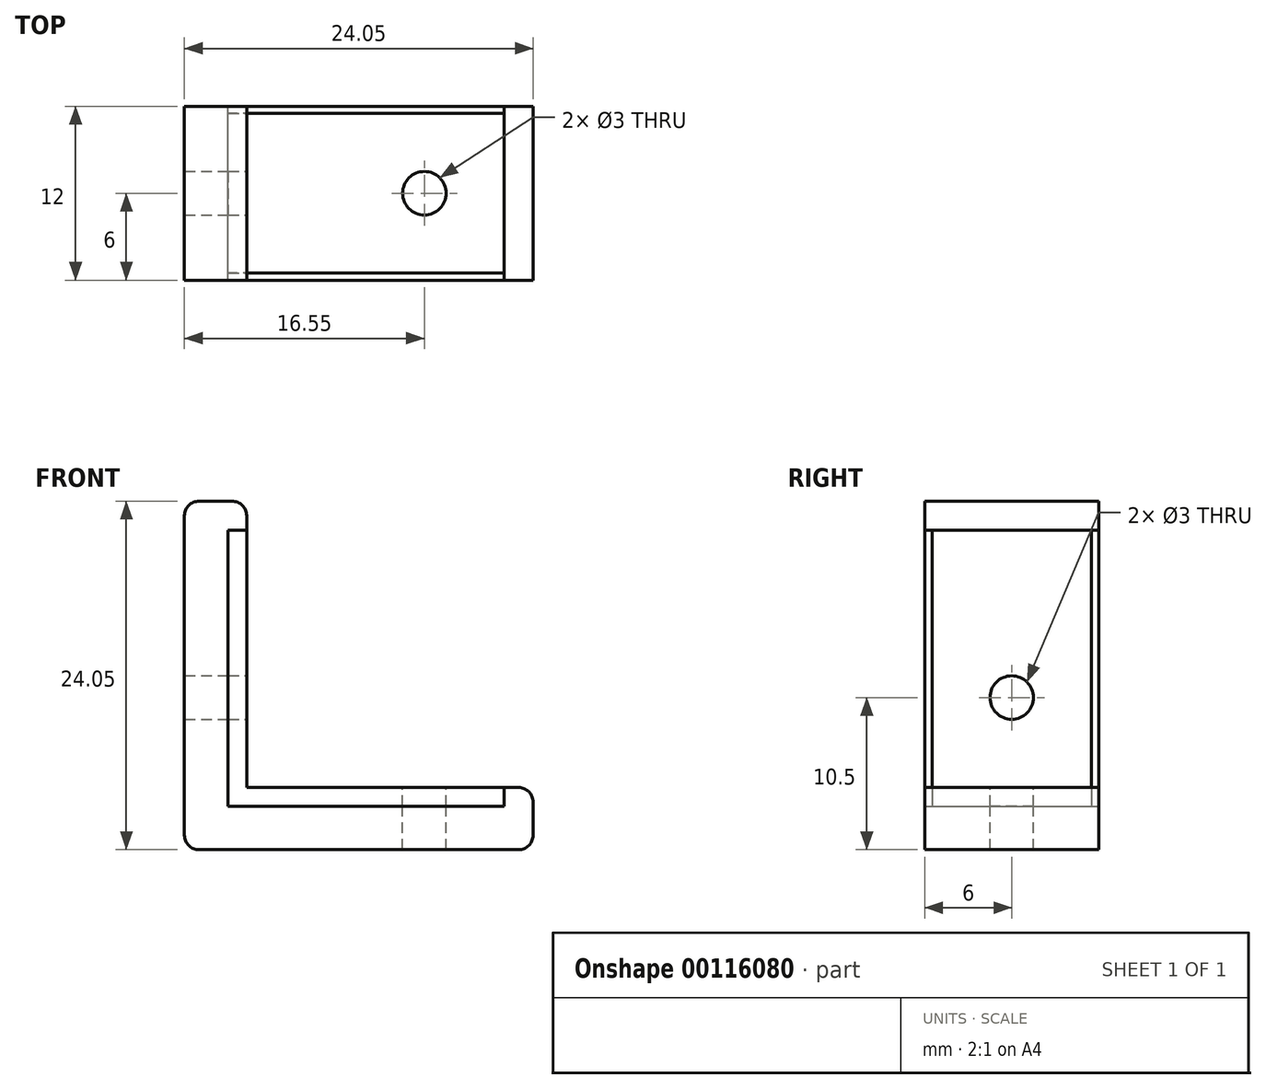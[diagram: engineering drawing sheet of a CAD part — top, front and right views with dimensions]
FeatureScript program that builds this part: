
annotation { "Feature Type Name" : "Feature", "Feature Type Description" : "" }
export const myFeature = defineFeature(function(context is Context, id is Id, definition is map)
    precondition{}
    {
        {
            var Q0;
            Q0=qCreatedBy(makeId("Front.planeOp"),FACE);
            var sketch = newSketch(context, id + "F0", { "sketchPlane" : qUnion([Q0])});
            skLineSegment(sketch, "E0", {"start": v(-29.8, 0) * mm, "end": v(29.8, 0) * mm, "construction": true});
            skLineSegment(sketch, "E1", {"start": v(-26.98, 7.5) * mm, "end": v(40.2, 7.5) * mm, "construction": true});
            skCircle(sketch, "E2", {"center": v(-26.98, 7.5) * mm, "radius": 2.6 * mm, "construction": true});
            skLineSegment(sketch, "E3.bottom", {"start": v(-17.5, 0) * mm, "end": v(17.5, 0) * mm});
            skLineSegment(sketch, "E3.top", {"start": v(-17.5, 6.35) * mm, "end": v(17.5, 6.35) * mm});
            skLineSegment(sketch, "E3.left", {"start": v(-17.5, 1.8) * mm, "end": v(-17.5, 6.35) * mm});
            skLineSegment(sketch, "E3.right", {"start": v(17.5, 0) * mm, "end": v(17.5, 6.35) * mm});
            skLineSegment(sketch, "E4.bottom", {"start": v(-17.4, 6.35) * mm, "end": v(-8.6, 6.35) * mm});
            skLineSegment(sketch, "E4.top", {"start": v(-17.4, 9.85) * mm, "end": v(-8.6, 9.85) * mm});
            skLineSegment(sketch, "E4.left", {"start": v(-17.4, 6.35) * mm, "end": v(-17.4, 9.85) * mm});
            skLineSegment(sketch, "E4.right", {"start": v(-8.6, 6.35) * mm, "end": v(-8.6, 9.85) * mm});
            skLineSegment(sketch, "E5", {"start": v(-13, 6.35) * mm, "end": v(-13, 0) * mm, "construction": true});
            skLineSegment(sketch, "E6", {"start": v(-10.5, 6.35) * mm, "end": v(-10.5, 0) * mm, "construction": true});
            skLineSegment(sketch, "E7.MirrorCS", {"start": v(-15.5, 6.35) * mm, "end": v(-15.5, 0) * mm, "construction": true});
            skLineSegment(sketch, "E8", {"start": v(-17.5, 1.8) * mm, "end": v(-7.5, 1.8) * mm});
            skLineSegment(sketch, "E9", {"start": v(-7.5, 1.8) * mm, "end": v(-7.5, 0) * mm});
            skLineSegment(sketch, "E10.bottom", {"start": v(-2.67, 0) * mm, "end": v(0, 0) * mm});
            skLineSegment(sketch, "E10.top", {"start": v(-2.67, 6.35) * mm, "end": v(0, 6.35) * mm});
            skLineSegment(sketch, "E10.left", {"start": v(-2.67, 0) * mm, "end": v(-2.67, 6.35) * mm});
            skLineSegment(sketch, "E10.right", {"start": v(0, 0) * mm, "end": v(0, 6.35) * mm});
            skLineSegment(sketch, "E11.bottom", {"start": v(9.83, 0) * mm, "end": v(12.5, 0) * mm});
            skLineSegment(sketch, "E11.top", {"start": v(9.83, 6.35) * mm, "end": v(12.5, 6.35) * mm});
            skLineSegment(sketch, "E11.left", {"start": v(9.83, 0) * mm, "end": v(9.83, 6.35) * mm});
            skLineSegment(sketch, "E11.right", {"start": v(12.5, 0) * mm, "end": v(12.5, 6.35) * mm});
            skCircle(sketch, "E12", {"center": v(-26.98, 7.5) * mm, "radius": 4.5 * mm, "construction": true});
            skSolve(sketch);
        }
        {
            var Q0;
            Q0=qCreatedBy(makeId("Front.planeOp"),FACE);
            var sketch = newSketch(context, id + "F1", { "sketchPlane" : qUnion([Q0])});
            skLineSegment(sketch, "E13.0", {"start": v(-7.5, 1.3) * mm, "end": v(-7.5, 0) * mm});
            skLineSegment(sketch, "E14.0", {"start": v(-25.26, 1.3) * mm, "end": v(-7.5, 1.3) * mm});
            skLineSegment(sketch, "E15.0", {"start": v(-25.26, 1.3) * mm, "end": v(-25.26, 19.05) * mm});
            skLineSegment(sketch, "E16", {"start": v(-7.5, 0) * mm, "end": v(-26.55, 0) * mm});
            skLineSegment(sketch, "E17", {"start": v(-26.55, 19.05) * mm, "end": v(-26.55, 0) * mm});
            skCircle(sketch, "E18.0", {"center": v(-26.98, 7.5) * mm, "radius": 4.5 * mm, "construction": true});
            skLineSegment(sketch, "E19", {"start": v(-34.52, 12) * mm, "end": v(-26.98, 12) * mm, "construction": true});
            skLineSegment(sketch, "E20", {"start": v(-26.55, 19.05) * mm, "end": v(-25.26, 19.05) * mm});
            skSolve(sketch);
        }
        {
            var Q0;
            Q0=makeQuery(id+"F1.imprint","IMPRINT",FACE,{"disambiguationData":[TD([[makeQuery(id+"F1.imprint","IMPRINT",EDGE,{"derivedFrom":sQuery(id+"F1.wireOp",EDGE,"E13.0")}),-1.0]])]});
            extrude(context, id + "F2", {"entities" : qUnion([Q0]), "endBound" : BoundingType.SYMMETRIC, "depth" : 11 * mm, "offsetDistance" : 25 * mm});
        }
        {
            var Q0;
            Q0=qCreatedBy(makeId("Front.planeOp"),FACE);
            var sketch = newSketch(context, id + "F3", { "sketchPlane" : qUnion([Q0])});
            skLineSegment(sketch, "E21.0", {"start": v(-25.26, 1.3) * mm, "end": v(-25.26, 21.05) * mm});
            skLineSegment(sketch, "E22.0", {"start": v(-25.26, 1.3) * mm, "end": v(-5.5, 1.3) * mm});
            skPoint(sketch, "E23.0", {"position": v(-7.5, 0.65) * mm});
            skLineSegment(sketch, "E24.0", {"start": v(-7.5, 1.3) * mm, "end": v(-7.5, 0) * mm});
            skPoint(sketch, "E25.0", {"position": v(-25.9, 19.05) * mm});
            skLineSegment(sketch, "E26.0", {"start": v(-26.55, 19.05) * mm, "end": v(-25.26, 19.05) * mm});
            skLineSegment(sketch, "E27.0", {"start": v(-22.26, 4.3) * mm, "end": v(-22.26, 19.05) * mm});
            skLineSegment(sketch, "E27.1", {"start": v(-22.26, 4.3) * mm, "end": v(-7.5, 4.3) * mm});
            skLineSegment(sketch, "E28", {"start": v(-22.26, 19.05) * mm, "end": v(-25.26, 19.05) * mm, "construction": true});
            skLineSegment(sketch, "E29", {"start": v(-7.5, 4.3) * mm, "end": v(-7.5, 1.3) * mm, "construction": true});
            skLineSegment(sketch, "E30", {"start": v(-7.5, 4.3) * mm, "end": v(-5.5, 4.3) * mm});
            skLineSegment(sketch, "E31", {"start": v(-5.5, 4.3) * mm, "end": v(-5.5, -3) * mm});
            skLineSegment(sketch, "E32", {"start": v(-5.5, 0) * mm, "end": v(-7.5, 0) * mm});
            skLineSegment(sketch, "E33", {"start": v(-22.26, 19.05) * mm, "end": v(-22.26, 21.05) * mm});
            skLineSegment(sketch, "E34", {"start": v(-22.26, 21.05) * mm, "end": v(-29.55, 21.05) * mm});
            skLineSegment(sketch, "E35", {"start": v(-26.55, 21.05) * mm, "end": v(-26.55, 19.05) * mm});
            skLineSegment(sketch, "E36.0", {"start": v(-29.55, 21.05) * mm, "end": v(-29.55, -3) * mm});
            skLineSegment(sketch, "E36.1", {"start": v(-5.5, -3) * mm, "end": v(-29.55, -3) * mm});
            skLineSegment(sketch, "E37.0", {"start": v(-26.55, 19.05) * mm, "end": v(-26.55, 0) * mm});
            skLineSegment(sketch, "E38.0", {"start": v(-7.5, 0) * mm, "end": v(-26.55, 0) * mm});
            skSolve(sketch);
        }
        {
            var Q0;
            {var subQ1=sQuery(id+"F3.wireOp",EDGE,"E32");Q0=makeQuery(id+"F3.imprint","IMPRINT",FACE,{"disambiguationData":[TD([[makeQuery(id+"F3.imprint","IMPRINT",EDGE,{"derivedFrom":subQ1}),1.0]])]});}
            var Q1;
            {var subQ3=sQuery(id+"F3.wireOp",EDGE,"E26.0");Q1=makeQuery(id+"F3.imprint","IMPRINT",FACE,{"disambiguationData":[TD([[makeQuery(id+"F3.imprint","IMPRINT",EDGE,{"derivedFrom":subQ3}),1.0]])]});}
            var Q2;
            {var subQ3=sQuery(id+"F3.wireOp",EDGE,"E24.0");Q2=makeQuery(id+"F3.imprint","IMPRINT",FACE,{"disambiguationData":[TD([[makeQuery(id+"F3.imprint","IMPRINT",EDGE,{"derivedFrom":subQ3}),1.0]])]});}
            extrude(context, id + "F4", {"entities" : qUnion([Q0, Q1, Q2]), "endBound" : BoundingType.SYMMETRIC, "depth" : 12 * mm, "offsetDistance" : 25 * mm});
        }
        {
            var Q0;
            Q0=makeQuery(id+"F2.opExtrude","SWEPT_FACE",FACE,{"disambiguationData":[OSD([sQuery(id+"F1.wireOp",EDGE,"E14.0")])]});
            var sketch = newSketch(context, id + "F5", { "sketchPlane" : qUnion([Q0])});
            skCircle(sketch, "E39", {"center": v(-13, 0) * mm, "radius": 1.5 * mm});
            skCircle(sketch, "E40", {"center": v(-13, 0) * mm, "radius": 2.6 * mm, "construction": true});
            skCircle(sketch, "E41", {"center": v(-13, 0) * mm, "radius": 4.5 * mm, "construction": true});
            skSolve(sketch);
        }
        {
            var Q0;
            Q0=makeQuery(id+"F5.imprint","IMPRINT",FACE,{"disambiguationData":[TD([[makeQuery(id+"F5.imprint","IMPRINT",EDGE,{"derivedFrom":sQuery(id+"F5.wireOp",EDGE,"E39")}),1.0]])]});
            var Q1;
            Q1=sQuery(id+"F5.wireOp",EDGE,"E40");
            var Q2;
            Q2=sQuery(id+"F5.wireOp",EDGE,"E39");
            extrude(context, id + "F6", {"entities" : qUnion([Q0]), "operationType" : NewBodyOperationType.REMOVE, "surfaceEntities" : qUnion([Q1, Q2]), "endBound" : BoundingType.SYMMETRIC, "oppositeDirection" : true, "depth" : 25 * mm, "offsetDistance" : 25 * mm});
        }
        {
            var Q0;
            Q0=makeQuery(id+"F2.opExtrude","SWEPT_FACE",FACE,{"disambiguationData":[OSD([sQuery(id+"F1.wireOp",EDGE,"E15.0"),sQuery(id+"F1.wireOp",EDGE,"JMiZOFVz-4SST-BxIo-qwsj-QiZxD8SXakA8")])]});
            var sketch = newSketch(context, id + "F7", { "sketchPlane" : qUnion([Q0])});
            skPoint(sketch, "E42.0", {"position": v(0, 7.5) * mm});
            skCircle(sketch, "E43", {"center": v(0, 7.5) * mm, "radius": 1.5 * mm});
            skCircle(sketch, "E44.cCircle", {"center": v(0, 7.5) * mm, "radius": 4.5 * mm, "construction": true});
            skLineSegment(sketch, "E44.0", {"start": v(4.5, 4.9) * mm, "end": v(0, 2.3) * mm});
            skLineSegment(sketch, "E44.1", {"start": v(0, 2.3) * mm, "end": v(-4.5, 4.9) * mm});
            skLineSegment(sketch, "E44.2", {"start": v(-4.5, 4.9) * mm, "end": v(-4.5, 10.1) * mm});
            skLineSegment(sketch, "E44.3", {"start": v(-4.5, 10.1) * mm, "end": v(0, 12.7) * mm});
            skLineSegment(sketch, "E44.4", {"start": v(0, 12.7) * mm, "end": v(4.5, 10.1) * mm});
            skLineSegment(sketch, "E44.5", {"start": v(4.5, 10.1) * mm, "end": v(4.5, 4.9) * mm});
            skPoint(sketch, "E44.0.midPoint", {"position": v(2.25, 3.6) * mm});
            skSolve(sketch);
        }
        {
            var Q0;
            Q0=makeQuery(id+"F7.imprint","IMPRINT",FACE,{"disambiguationData":[TD([[makeQuery(id+"F7.imprint","IMPRINT",EDGE,{"derivedFrom":sQuery(id+"F7.wireOp",EDGE,"E43")}),1.0]])]});
            extrude(context, id + "F8", {"entities" : qUnion([Q0]), "operationType" : NewBodyOperationType.REMOVE, "endBound" : BoundingType.SYMMETRIC, "oppositeDirection" : true, "depth" : 25 * mm, "offsetDistance" : 25 * mm});
        }
        {
            var Q0;
            Q0=makeQuery(id+"F4.opExtrude","SWEPT_EDGE",EDGE,{"disambiguationData":[OSD([sQuery(id+"F3.wireOp",EDGE,"E21.0"),sQuery(id+"F3.wireOp",EDGE,"E34")])]});
            var Q1;
            Q1=makeQuery(id+"F4.opExtrude","SWEPT_EDGE",EDGE,{"disambiguationData":[OSD([sQuery(id+"F3.wireOp",EDGE,"E22.0"),sQuery(id+"F3.wireOp",EDGE,"E31")])]});
            var Q2;
            Q2=makeQuery(id+"F4.opExtrude","SWEPT_EDGE",EDGE,{"disambiguationData":[OSD([sQuery(id+"F3.wireOp",EDGE,"E34"),sQuery(id+"F3.wireOp",EDGE,"E36.0")])]});
            var Q3;
            Q3=makeQuery(id+"F4.opExtrude","SWEPT_EDGE",EDGE,{"disambiguationData":[OSD([sQuery(id+"F3.wireOp",EDGE,"E31"),sQuery(id+"F3.wireOp",EDGE,"E36.1")])]});
            var Q4;
            Q4=makeQuery(id+"F4.opExtrude","SWEPT_EDGE",EDGE,{"disambiguationData":[OSD([sQuery(id+"F3.wireOp",EDGE,"E36.0"),sQuery(id+"F3.wireOp",EDGE,"E36.1")])]});
            fillet(context, id + "F9", {"entities" : qUnion([Q0, Q1, Q2, Q3, Q4]), "radius" : 1 * mm, "tangentPropagation" : true, "allowEdgeOverflow" : false});
        }
    });
